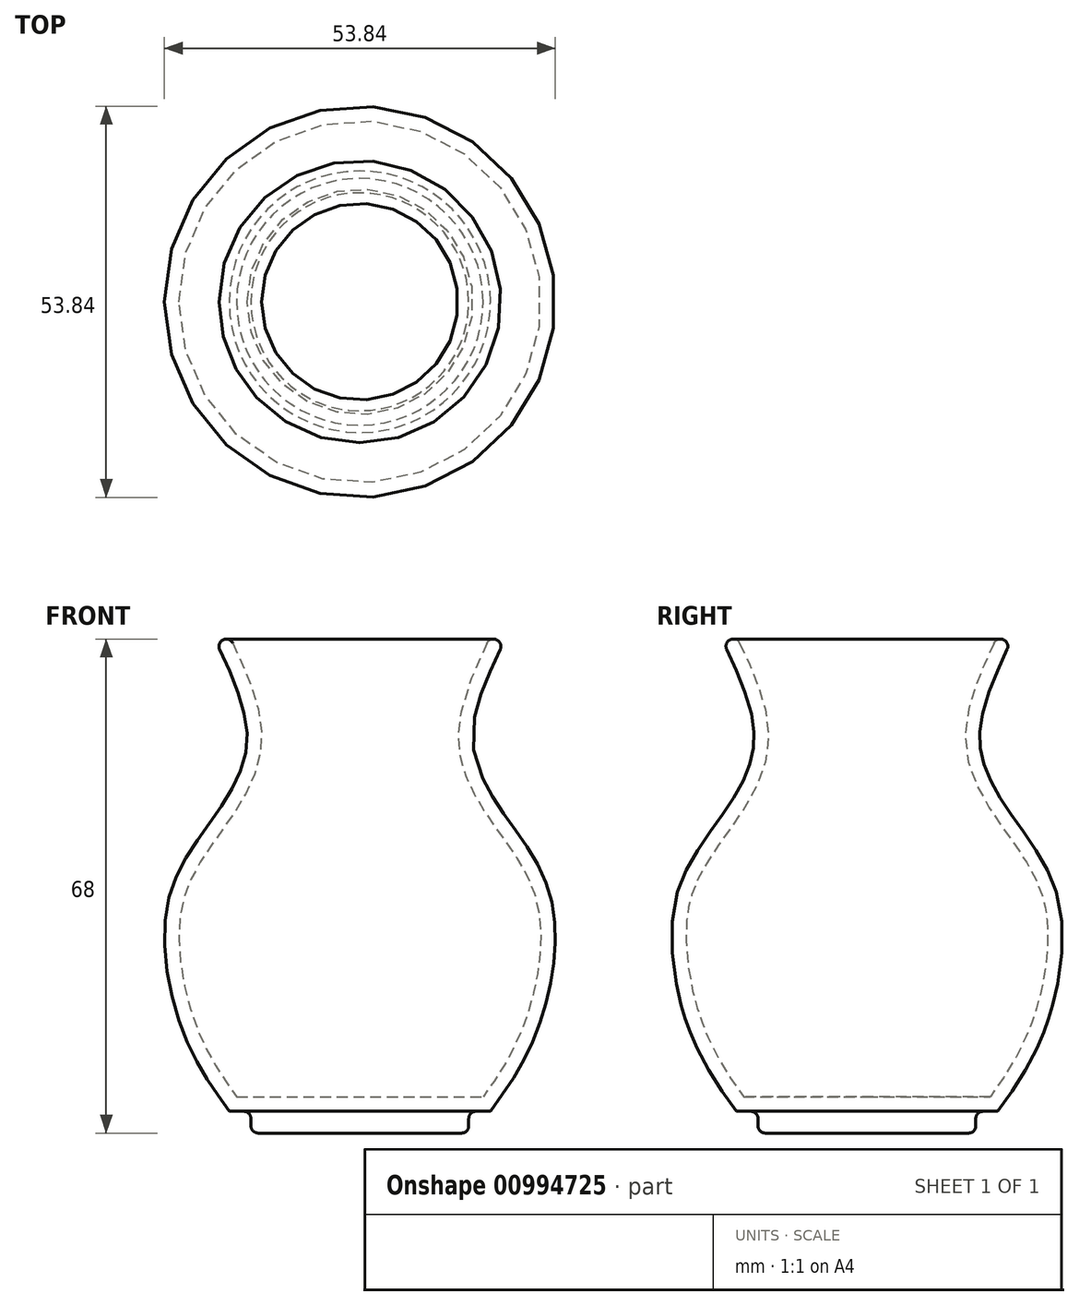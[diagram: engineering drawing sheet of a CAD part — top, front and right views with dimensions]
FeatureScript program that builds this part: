
annotation { "Feature Type Name" : "Feature", "Feature Type Description" : "" }
export const myFeature = defineFeature(function(context is Context, id is Id, definition is map)
    precondition{}
    {
        {
            var Q0;
            Q0=qCreatedBy(makeId("Front.planeOp"),FACE);
            var sketch = newSketch(context, id + "F0", { "sketchPlane" : qUnion([Q0])});
            skLineSegment(sketch, "E0", {"start": v(0, 0) * mm, "end": v(0, 65) * mm});
            skLineSegment(sketch, "E1", {"start": v(0, 65) * mm, "end": v(20, 65) * mm});
            skLineSegment(sketch, "E2", {"start": v(0, 0) * mm, "end": v(18, 0) * mm});
            skFitSpline(sketch, "E3", {"points": [v(20, 65) * mm, v(15.54, 51.12) * mm, v(20, 40.68) * mm, v(26.45, 28.82) * mm, v(24.31, 10.8) * mm, v(18, 0) * mm], "startDerivative": vector(-33.73, -70.4) * mm, "endDerivative": vector(-36.3, -50.31) * mm});
            skSolve(sketch);
        }
        {
            var Q0;
            Q0 = qSketchRegion(id + "F0", true);
            var Q1;
            Q1=sQuery(id+"F0.wireOp",EDGE,"E0");
            revolve(context, id + "F1", {"surfaceOperationType" : NewSurfaceOperationType.NEW, "entities" : qUnion([Q0]), "axis" : qUnion([Q1]), "revolveType" : RevolveType.FULL});
        }
        {
            var Q0;
            Q0=makeQuery(id+"F1.opRevolve","SWEPT_FACE",FACE,{"disambiguationData":[OSD([sQuery(id+"F0.wireOp",EDGE,"E1")])]});
            shell(context, id + "F2", {"entities" : qUnion([Q0]), "thickness" : 2 * mm});
        }
        {
            var Q0;
            Q0=makeQuery(id+"F1.opRevolve","SWEPT_FACE",FACE,{"disambiguationData":[OSD([sQuery(id+"F0.wireOp",EDGE,"E2")])]});
            var sketch = newSketch(context, id + "F3", { "sketchPlane" : qUnion([Q0])});
            skCircle(sketch, "E4.0", {"center": v(0, 0) * mm, "radius": 15 * mm});
            skSolve(sketch);
        }
        {
            var Q0;
            Q0 = qSketchRegion(id + "F3", true);
            extrude(context, id + "F4", {"entities" : qUnion([Q0]), "operationType" : NewBodyOperationType.ADD, "depth" : 3 * mm, "offsetDistance" : 25 * mm});
        }
        {
            var Q0;
            Q0=makeQuery(id+"F4.opExtrude","SWEPT_FACE",FACE,{"disambiguationData":[OSD([sQuery(id+"F3.wireOp",EDGE,"E4.0")])]});
            var Q1;
            Q1=makeQuery(id+"F1.opRevolve","SWEPT_FACE",FACE,{"disambiguationData":[OSD([sQuery(id+"F0.wireOp",EDGE,"E1")])]});
            fillet(context, id + "F5", {"entities" : qUnion([Q0, Q1]), "radius" : 1 * mm, "tangentPropagation" : true, "allowEdgeOverflow" : false});
        }
    });
